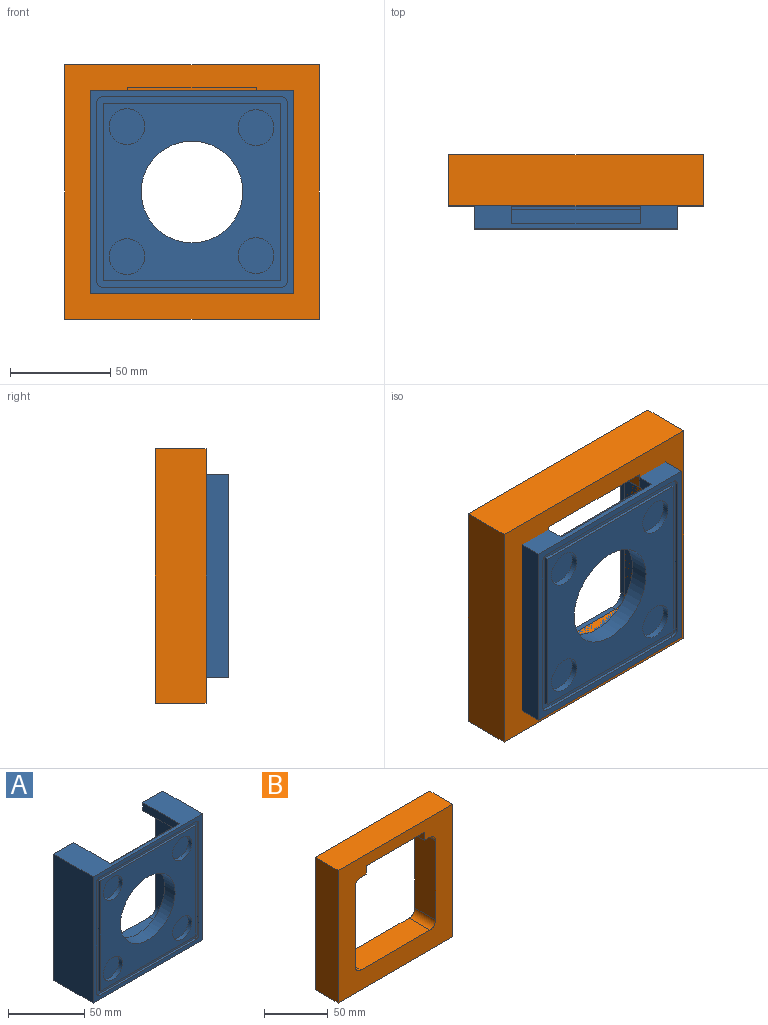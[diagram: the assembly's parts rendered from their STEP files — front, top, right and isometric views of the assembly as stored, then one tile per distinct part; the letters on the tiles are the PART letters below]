
ASSEMBLY  parts=2 mates=1
PART A: 43 faces, bbox 101.6x36.8x101.6 mm
  f0: cylinder r=25.4mm len=50.8mm, axis (0,-1,0), area 1520.1mm2, adj f19,f33
  f1: plane 101.6x101.6mm, normal (0,-1,0), area 1258.7mm2, adj f2,f3,f4,f5,f9,f10,f11,f12
  f2: plane 101.6x36.8mm, normal (0,0,1), area 1536.3mm2, adj f1,f3,f5,f28,f29,f30,f31
  f3: plane 101.6x36.8mm, normal (-1,0,0), area 3739.3mm2, adj f1,f2,f4,f28
  f4: plane 101.6x36.8mm, normal (0,0,-1), area 3739.3mm2, adj f1,f3,f5,f28
  f5: plane 101.6x36.8mm, normal (1,0,0), area 3739.3mm2, adj f1,f2,f4,f28
  f6: plane 88.9x1.59mm, normal (0,0,1), area 141.1mm2, adj f7,f17,f18,f19
  f7: plane 88.9x1.59mm, normal (1,0,0), area 141.1mm2, adj f6,f8,f18,f19
  f8: plane 88.9x1.59mm, normal (0,0,-1), area 141.1mm2, adj f7,f17,f18,f19
  f9: plane 88.9x1.59mm, normal (-1,0,0), area 141.1mm2, adj f1,f10,f16,f18
  f10: cylinder r=3.17mm len=3.18mm, axis (0,-1,0), area 7.9mm2, adj f1,f9,f11,f18
  f11: plane 88.9x1.59mm, normal (0,0,-1), area 141.1mm2, adj f1,f10,f12,f18
  f12: cylinder r=3.17mm len=3.18mm, axis (0,-1,0), area 7.9mm2, adj f1,f11,f13,f18
  f13: plane 88.9x1.59mm, normal (1,0,0), area 141.1mm2, adj f1,f12,f14,f18
  f14: cylinder r=3.17mm len=3.18mm, axis (0,-1,0), area 7.9mm2, adj f1,f13,f15,f18
  f15: plane 88.9x1.59mm, normal (0,0,1), area 141.1mm2, adj f1,f14,f16,f18
  f16: cylinder r=3.17mm len=3.18mm, axis (0,-1,0), area 7.9mm2, adj f1,f9,f15,f18
  f17: plane 88.9x1.59mm, normal (-1,0,0), area 141.1mm2, adj f6,f8,f18,f19
  f18: plane 95.25x95.25mm, normal (0,-1,0), area 1160.7mm2, adj f6,f7,f8,f9,f10,f11,f12,f13
  f19: plane 88.9x88.9mm, normal (0,-1,0), area 4876.6mm2, adj f0,f6,f7,f8,f17,f20,f21,f22
  f20: cylinder r=8.92mm len=17.84mm, axis (0,1,0), area 177.9mm2, adj f19,f24
  f21: cylinder r=8.92mm len=17.84mm, axis (0,1,0), area 177.9mm2, adj f19,f25
  f22: cylinder r=8.92mm len=17.84mm, axis (0,1,0), area 177.9mm2, adj f19,f26
  f23: cylinder r=8.92mm len=17.84mm, axis (0,1,0), area 177.9mm2, adj f19,f27
  f24: plane 17.84x17.84mm, normal (0,-1,0), area 249.9mm2, adj f20
  f25: plane 17.84x17.84mm, normal (0,-1,0), area 249.9mm2, adj f21
  f26: plane 17.84x17.84mm, normal (0,-1,0), area 249.9mm2, adj f22
  f27: plane 17.84x17.84mm, normal (0,-1,0), area 249.9mm2, adj f23
  f28: plane 101.6x101.6mm, normal (0,1,0), area 2045.7mm2, adj f2,f3,f4,f5,f30,f31,f34,f35
  f29: plane 64.29x6.35mm, normal (0,1,0), area 408.3mm2, adj f2,f30,f31,f32
  f30: plane 34.26x6.35mm, normal (-1,0,0), area 217.6mm2, adj f2,f28,f29,f32,f35
  f31: plane 34.26x6.35mm, normal (1,0,0), area 217.6mm2, adj f2,f28,f29,f32,f36
  f32: plane 64.29x6.99mm, normal (0,0,1), area 449.1mm2, adj f29,f30,f31,f33
  f33: plane 88.9x88.9mm, normal (0,1,0), area 5841.8mm2, adj f0,f32,f34,f35,f36,f37,f38,f39
  f34: cylinder r=6.35mm len=27.28mm, axis (0,1,0), area 272.1mm2, adj f28,f33,f36,f42
  f35: plane 27.28x5.95mm, normal (0,0,-1), area 162.4mm2, adj f28,f30,f33,f37
  f36: plane 27.28x5.95mm, normal (0,0,-1), area 162.4mm2, adj f28,f31,f33,f34
  f37: cylinder r=6.35mm len=27.28mm, axis (0,1,0), area 272.1mm2, adj f28,f33,f35,f38
  f38: plane 76.2x27.28mm, normal (-1,0,0), area 2078.7mm2, adj f28,f33,f37,f39
  f39: cylinder r=6.35mm len=27.28mm, axis (0,1,0), area 272.1mm2, adj f28,f33,f38,f40
  f40: plane 76.2x27.28mm, normal (0,0,1), area 2078.7mm2, adj f28,f33,f39,f41
  f41: cylinder r=6.35mm len=27.28mm, axis (0,1,0), area 272.1mm2, adj f28,f33,f40,f42
  f42: plane 76.2x27.28mm, normal (1,0,0), area 2078.7mm2, adj f28,f33,f34,f41
PART B: 27 faces, bbox 127x25.4x127 mm
  f0: plane 127x127mm, normal (0,1,0), area 4853.2mm2, adj f10,f11,f12,f13,f19,f20,f21,f22
  f1: plane 76.2x23.02mm, normal (0,0,-1), area 333.7mm2, adj f2,f3,f9,f14,f15,f16,f18
  f2: cylinder r=6.35mm len=23.02mm, axis (0,1,0), area 229.6mm2, adj f1,f8,f9,f18
  f3: cylinder r=6.35mm len=23.02mm, axis (0,1,0), area 229.6mm2, adj f1,f4,f9,f18
  f4: plane 76.2x23.02mm, normal (-1,0,0), area 1754mm2, adj f3,f5,f9,f18
  f5: cylinder r=6.35mm len=23.02mm, axis (0,1,0), area 229.6mm2, adj f4,f6,f9,f18
  f6: plane 76.2x23.02mm, normal (0,0,1), area 1754mm2, adj f5,f7,f9,f18
  f7: cylinder r=6.35mm len=23.02mm, axis (0,1,0), area 229.6mm2, adj f6,f8,f9,f18
  f8: plane 76.2x23.02mm, normal (1,0,0), area 1754mm2, adj f2,f7,f9,f18
  f9: plane 127x127mm, normal (0,-1,0), area 7750.1mm2, adj f1,f2,f3,f4,f5,f6,f7,f8
  f10: plane 127x25.4mm, normal (-1,0,0), area 3225.8mm2, adj f0,f9,f11,f13
  f11: plane 127x25.4mm, normal (0,0,1), area 3225.8mm2, adj f0,f9,f10,f12
  f12: plane 127x25.4mm, normal (1,0,0), area 3225.8mm2, adj f0,f9,f11,f13
  f13: plane 127x25.4mm, normal (0,0,-1), area 3225.8mm2, adj f0,f9,f10,f12
  f14: plane 22.09x7.94mm, normal (-1,0,0), area 175.4mm2, adj f1,f9,f15,f17
  f15: plane 64.29x7.94mm, normal (0,-1,0), area 510.3mm2, adj f1,f14,f16,f17
  f16: plane 22.09x7.94mm, normal (1,0,0), area 175.4mm2, adj f1,f9,f15,f17
  f17: plane 64.29x22.09mm, normal (0,0,-1), area 1420.4mm2, adj f9,f14,f15,f16
  f18: plane 107.95x104.78mm, normal (0,1,0), area 3407.3mm2, adj f1,f2,f3,f4,f5,f6,f7,f8
  f19: plane 95.25x2.38mm, normal (1,0,0), area 226.8mm2, adj f0,f18,f20,f26
  f20: cylinder r=6.35mm len=6.35mm, axis (0,1,0), area 23.8mm2, adj f0,f18,f19,f21
  f21: plane 92.08x2.38mm, normal (0,0,-1), area 219.3mm2, adj f0,f18,f20,f22
  f22: cylinder r=6.35mm len=6.35mm, axis (0,1,0), area 23.8mm2, adj f0,f18,f21,f23
  f23: plane 95.25x2.38mm, normal (-1,0,0), area 226.8mm2, adj f0,f18,f22,f24
  f24: cylinder r=6.35mm len=6.35mm, axis (0,1,0), area 23.8mm2, adj f0,f18,f23,f25
  f25: plane 92.08x2.38mm, normal (0,0,1), area 219.3mm2, adj f0,f18,f24,f26
  f26: cylinder r=6.35mm len=6.35mm, axis (0,1,0), area 23.8mm2, adj f0,f18,f19,f25
PLACE A t=(90.14,14.18,-23.45)mm
PLACE B t=(90.14,-11.22,-23.45)mm
MATE planar B.f0 <-> A.f28  axis (0,1,0) through (90.14,50.99,-23.45)mm
